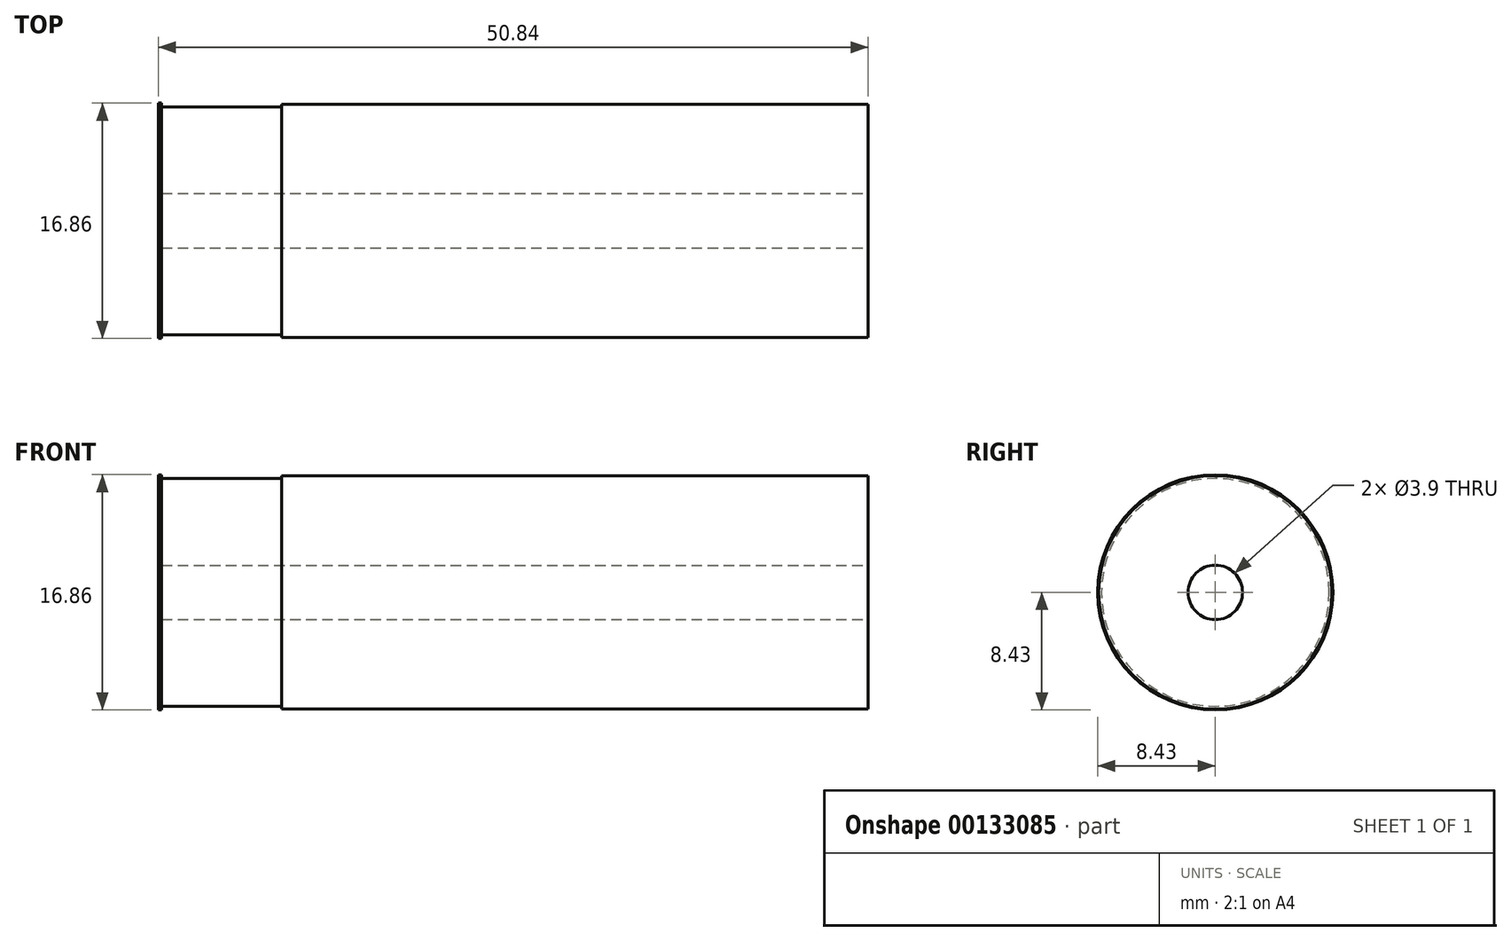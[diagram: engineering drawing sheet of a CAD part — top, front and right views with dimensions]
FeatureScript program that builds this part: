
annotation { "Feature Type Name" : "Feature", "Feature Type Description" : "" }
export const myFeature = defineFeature(function(context is Context, id is Id, definition is map)
    precondition{}
    {
        {
            var Q0;
            Q0=qCreatedBy(makeId("Top.planeOp"),FACE);
            var sketch = newSketch(context, id + "F0", { "sketchPlane" : qUnion([Q0])});
            skPoint(sketch, "E0.middle", {"position": v(0, 0) * mm});
            skLineSegment(sketch, "E1.bottom", {"start": v(0, 0) * mm, "end": v(42, 0) * mm});
            skLineSegment(sketch, "E1.top", {"start": v(0, 8.35) * mm, "end": v(42, 8.35) * mm});
            skLineSegment(sketch, "E1.left", {"start": v(0, 0) * mm, "end": v(0, 8.35) * mm});
            skLineSegment(sketch, "E1.right", {"start": v(42, 0) * mm, "end": v(42, 8.35) * mm});
            skSolve(sketch);
        }
        {
            var Q0;
            Q0=makeQuery(id+"F0.imprint","IMPRINT",FACE,{"disambiguationData":[TD([[makeQuery(id+"F0.imprint","IMPRINT",EDGE,{"derivedFrom":sQuery(id+"F0.wireOp",EDGE,"E1.bottom")}),1.0]])]});
            var Q1;
            Q1=sQuery(id+"F0.wireOp",EDGE,"E1.bottom");
            revolve(context, id + "F1", {"entities" : qUnion([Q0]), "axis" : qUnion([Q1]), "revolveType" : RevolveType.FULL});
        }
        {
            var Q0;
            Q0=qCreatedBy(makeId("Top.planeOp"),FACE);
            var sketch = newSketch(context, id + "F2", { "sketchPlane" : qUnion([Q0])});
            skLineSegment(sketch, "E2.bottom", {"start": v(0, 0) * mm, "end": v(-8.6, 0) * mm});
            skLineSegment(sketch, "E2.top", {"start": v(0, 8.16) * mm, "end": v(-8.6, 8.16) * mm});
            skLineSegment(sketch, "E2.left", {"start": v(0, 0) * mm, "end": v(0, 8.16) * mm});
            skLineSegment(sketch, "E2.right", {"start": v(-8.6, 0) * mm, "end": v(-8.6, 8.16) * mm});
            skSolve(sketch);
        }
        {
            var Q0;
            Q0 = qSketchRegion(id + "F2", true);
            var Q1;
            Q1=sQuery(id+"F2.wireOp",EDGE,"E2.bottom");
            revolve(context, id + "F3", {"operationType" : NewBodyOperationType.ADD, "entities" : qUnion([Q0]), "axis" : qUnion([Q1]), "revolveType" : RevolveType.FULL});
        }
        {
            var Q0;
            Q0=qCreatedBy(makeId("Top.planeOp"),FACE);
            var sketch = newSketch(context, id + "F4", { "sketchPlane" : qUnion([Q0])});
            skLineSegment(sketch, "E3.bottom", {"start": v(-8.6, 0) * mm, "end": v(-8.84, 0) * mm});
            skLineSegment(sketch, "E3.top", {"start": v(-8.6, 8.43) * mm, "end": v(-8.84, 8.43) * mm});
            skLineSegment(sketch, "E3.left", {"start": v(-8.6, 0) * mm, "end": v(-8.6, 8.43) * mm});
            skLineSegment(sketch, "E3.right", {"start": v(-8.84, 0) * mm, "end": v(-8.84, 8.43) * mm});
            skSolve(sketch);
        }
        {
            var Q0;
            Q0 = qSketchRegion(id + "F4", true);
            var Q1;
            Q1=sQuery(id+"F4.wireOp",EDGE,"E3.bottom");
            revolve(context, id + "F5", {"operationType" : NewBodyOperationType.ADD, "entities" : qUnion([Q0]), "axis" : qUnion([Q1]), "revolveType" : RevolveType.FULL});
        }
        {
            var Q0;
            Q0=makeQuery(id+"F1.opRevolve","SWEPT_FACE",FACE,{"disambiguationData":[OSD([sQuery(id+"F0.wireOp",EDGE,"E1.right")])]});
            var sketch = newSketch(context, id + "F6", { "sketchPlane" : qUnion([Q0])});
            skCircle(sketch, "E4", {"center": v(0, 0) * mm, "radius": 1.95 * mm});
            skSolve(sketch);
        }
        {
            var Q0;
            Q0 = qSketchRegion(id + "F6", true);
            extrude(context, id + "F7", {"entities" : qUnion([Q0]), "operationType" : NewBodyOperationType.REMOVE, "oppositeDirection" : true, "depth" : 54.72 * mm});
        }
    });
